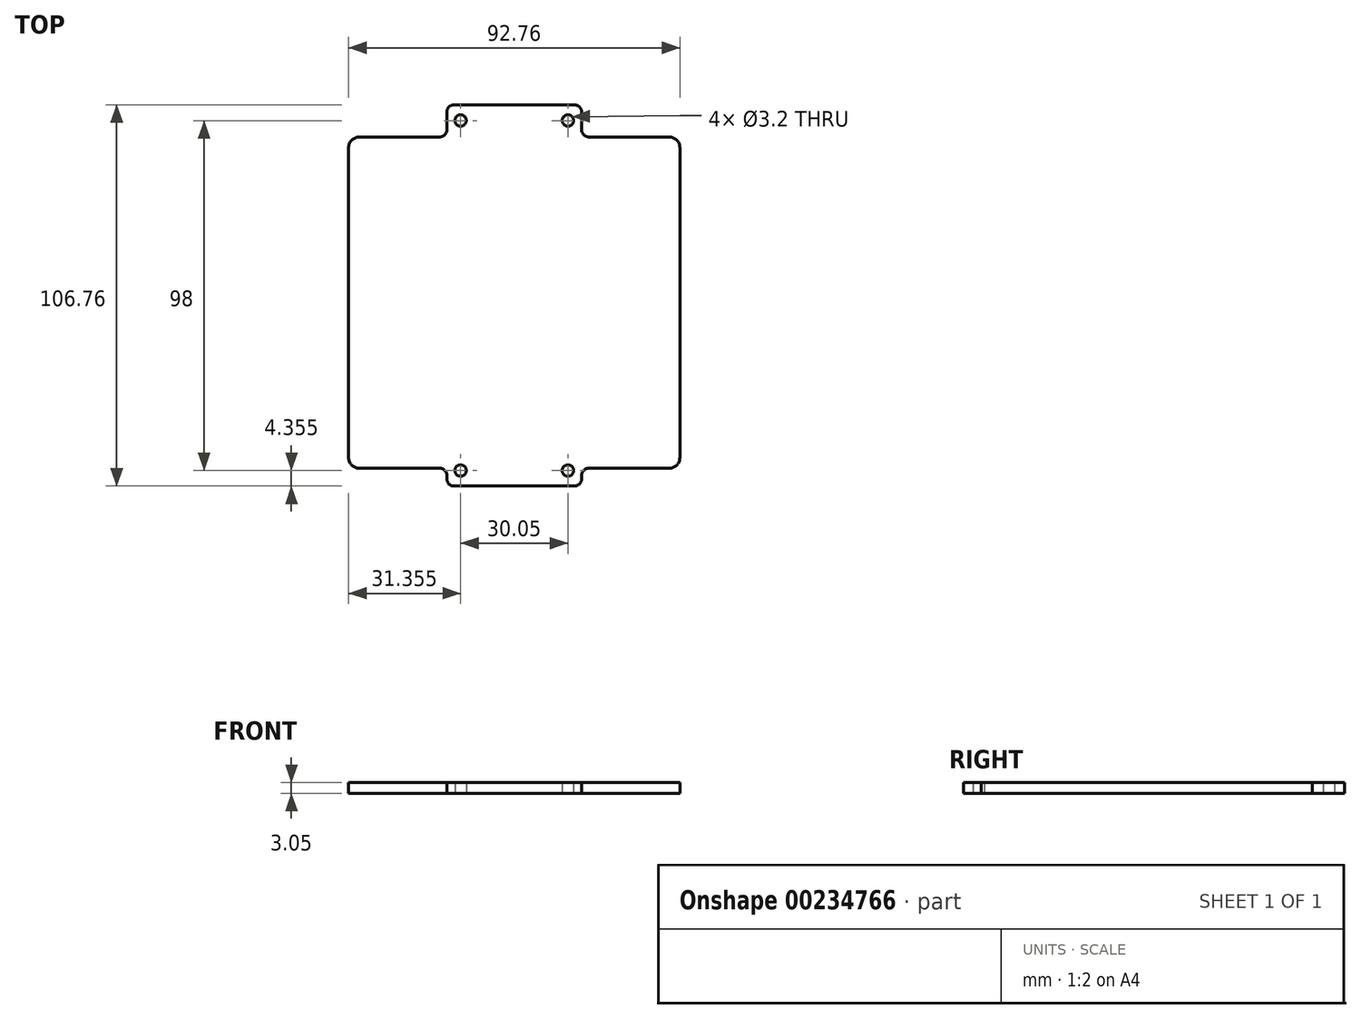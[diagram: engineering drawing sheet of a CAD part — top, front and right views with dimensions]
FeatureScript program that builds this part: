
annotation { "Feature Type Name" : "Feature", "Feature Type Description" : "" }
export const myFeature = defineFeature(function(context is Context, id is Id, definition is map)
    precondition{}
    {
        {
            var Q0;
            Q0=qCreatedBy(makeId("Top.planeOp"),FACE);
            var sketch = newSketch(context, id + "F0", { "sketchPlane" : qUnion([Q0])});
            skLineSegment(sketch, "E0.bottom", {"start": v(-46.38, 46.37) * mm, "end": v(46.38, 46.37) * mm});
            skLineSegment(sketch, "E0.top", {"start": v(-46.38, -46.37) * mm, "end": v(46.37, -46.37) * mm});
            skLineSegment(sketch, "E0.left", {"start": v(-46.38, 46.38) * mm, "end": v(-46.38, -46.37) * mm});
            skLineSegment(sketch, "E0.right", {"start": v(46.38, 46.38) * mm, "end": v(46.37, -46.37) * mm});
            skPoint(sketch, "E0.middle", {"position": v(0, 0) * mm});
            skLineSegment(sketch, "E1.bottom", {"start": v(-18.88, 55.38) * mm, "end": v(18.88, 55.38) * mm});
            skLineSegment(sketch, "E1.top", {"start": v(-18.88, 46.38) * mm, "end": v(18.88, 46.38) * mm});
            skLineSegment(sketch, "E1.left", {"start": v(-18.88, 55.38) * mm, "end": v(-18.88, 46.37) * mm});
            skLineSegment(sketch, "E1.right", {"start": v(18.88, 55.38) * mm, "end": v(18.88, 46.37) * mm});
            skPoint(sketch, "E1.middle", {"position": v(0, 50.87) * mm});
            skLineSegment(sketch, "E2.bottom", {"start": v(-18.87, -46.38) * mm, "end": v(18.88, -46.38) * mm});
            skLineSegment(sketch, "E2.top", {"start": v(-18.88, -51.38) * mm, "end": v(18.88, -51.38) * mm});
            skLineSegment(sketch, "E2.left", {"start": v(-18.88, -46.38) * mm, "end": v(-18.88, -51.38) * mm});
            skLineSegment(sketch, "E2.right", {"start": v(18.88, -46.38) * mm, "end": v(18.88, -51.38) * mm});
            skPoint(sketch, "E2.middle", {"position": v(0, -48.88) * mm});
            skCircle(sketch, "E3", {"center": v(-15.03, 50.98) * mm, "radius": 1.6 * mm});
            skCircle(sketch, "E4.MirrorC", {"center": v(15.03, 50.98) * mm, "radius": 1.6 * mm});
            skCircle(sketch, "E5", {"center": v(15.03, -47.03) * mm, "radius": 1.6 * mm});
            skCircle(sketch, "E6.MirrorC", {"center": v(-15.03, -47.03) * mm, "radius": 1.6 * mm});
            skSolve(sketch);
        }
        {
            var Q0;
            {var subQ6=sQuery(id+"F0.wireOp",EDGE,"E0.left");Q0=makeQuery(id+"F0.imprint","IMPRINT",FACE,{"disambiguationData":[TD([[makeQuery(id+"F0.imprint","IMPRINT",EDGE,{"derivedFrom":subQ6}),1.0]])]});}
            var Q1;
            Q1=makeQuery(id+"F0.imprint","IMPRINT",FACE,{"disambiguationData":[TD([[makeQuery(id+"F0.imprint","IMPRINT",EDGE,{"derivedFrom":sQuery(id+"F0.wireOp",EDGE,"E2.top")}),1.0]])]});
            var Q2;
            Q2=makeQuery(id+"F0.imprint","IMPRINT",FACE,{"disambiguationData":[TD([[makeQuery(id+"F0.imprint","IMPRINT",EDGE,{"derivedFrom":sQuery(id+"F0.wireOp",EDGE,"E1.bottom")}),-1.0]])]});
            extrude(context, id + "F1", {"entities" : qUnion([Q0, Q1, Q2]), "depth" : 3.05 * mm});
        }
        {
            var Q0;
            Q0=makeQuery(id+"F1.opExtrude","SWEPT_EDGE",EDGE,{"disambiguationData":[OSD([sQuery(id+"F0.wireOp",EDGE,"E0.bottom"),sQuery(id+"F0.wireOp",EDGE,"E1.top"),sQuery(id+"F0.wireOp",EDGE,"E1.right")])]});
            var Q1;
            Q1=makeQuery(id+"F1.opExtrude","SWEPT_EDGE",EDGE,{"disambiguationData":[OSD([sQuery(id+"F0.wireOp",EDGE,"E0.bottom"),sQuery(id+"F0.wireOp",EDGE,"E1.top"),sQuery(id+"F0.wireOp",EDGE,"E1.left")])]});
            var Q2;
            Q2=makeQuery(id+"F1.opExtrude","SWEPT_EDGE",EDGE,{"disambiguationData":[OSD([sQuery(id+"F0.wireOp",EDGE,"E0.top"),sQuery(id+"F0.wireOp",EDGE,"E2.bottom"),sQuery(id+"F0.wireOp",EDGE,"E2.left")])]});
            var Q3;
            Q3=makeQuery(id+"F1.opExtrude","SWEPT_EDGE",EDGE,{"disambiguationData":[OSD([sQuery(id+"F0.wireOp",EDGE,"E0.top"),sQuery(id+"F0.wireOp",EDGE,"E2.bottom"),sQuery(id+"F0.wireOp",EDGE,"E2.right")])]});
            var Q4;
            Q4=makeQuery(id+"F1.opExtrude","SWEPT_EDGE",EDGE,{"disambiguationData":[OSD([sQuery(id+"F0.wireOp",EDGE,"E1.bottom"),sQuery(id+"F0.wireOp",EDGE,"E1.left")])]});
            var Q5;
            Q5=makeQuery(id+"F1.opExtrude","SWEPT_EDGE",EDGE,{"disambiguationData":[OSD([sQuery(id+"F0.wireOp",EDGE,"E1.bottom"),sQuery(id+"F0.wireOp",EDGE,"E1.right")])]});
            var Q6;
            Q6=makeQuery(id+"F1.opExtrude","SWEPT_EDGE",EDGE,{"disambiguationData":[OSD([sQuery(id+"F0.wireOp",EDGE,"E2.top"),sQuery(id+"F0.wireOp",EDGE,"E2.right")])]});
            var Q7;
            Q7=makeQuery(id+"F1.opExtrude","SWEPT_EDGE",EDGE,{"disambiguationData":[OSD([sQuery(id+"F0.wireOp",EDGE,"E2.top"),sQuery(id+"F0.wireOp",EDGE,"E2.left")])]});
            fillet(context, id + "F2", {"entities" : qUnion([Q0, Q1, Q2, Q3, Q4, Q5, Q6, Q7]), "radius" : 2 * mm, "tangentPropagation" : true, "allowEdgeOverflow" : false});
        }
        {
            var Q0;
            Q0=makeQuery(id+"F1.opExtrude","SWEPT_EDGE",EDGE,{"disambiguationData":[OSD([sQuery(id+"F0.wireOp",EDGE,"E0.top"),sQuery(id+"F0.wireOp",EDGE,"E0.left")])]});
            var Q1;
            Q1=makeQuery(id+"F1.opExtrude","SWEPT_EDGE",EDGE,{"disambiguationData":[OSD([sQuery(id+"F0.wireOp",EDGE,"E0.top"),sQuery(id+"F0.wireOp",EDGE,"E0.right")])]});
            var Q2;
            Q2=makeQuery(id+"F1.opExtrude","SWEPT_EDGE",EDGE,{"disambiguationData":[OSD([sQuery(id+"F0.wireOp",EDGE,"E0.bottom"),sQuery(id+"F0.wireOp",EDGE,"E0.right")])]});
            var Q3;
            Q3=makeQuery(id+"F1.opExtrude","SWEPT_EDGE",EDGE,{"disambiguationData":[OSD([sQuery(id+"F0.wireOp",EDGE,"E0.bottom"),sQuery(id+"F0.wireOp",EDGE,"E0.left")])]});
            fillet(context, id + "F3", {"entities" : qUnion([Q0, Q1, Q2, Q3]), "radius" : 3 * mm, "tangentPropagation" : true, "allowEdgeOverflow" : false});
        }
    });
